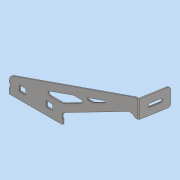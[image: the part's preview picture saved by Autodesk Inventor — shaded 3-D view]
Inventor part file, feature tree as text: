
AUTODESK INVENTOR PART (.ipt)
format: ipt  version: 2020 (Build 240168000, 168)  size: 465,920 bytes
history: native  units: mm
features: other x3, extrude x1, plane x1
ambient origin geometry x8: Origin, YZ Plane, XZ Plane, XY Plane, X Axis, Y Axis, Z Axis, Center Point
bodies: Body1 (feature_tree)
feature tree (5):
  other  "實體1"
  extrude  "擠出1"  Depth=130.0mm
  other  "折彎零件1"
  plane  "工作平面1"
  other  "定義1"
